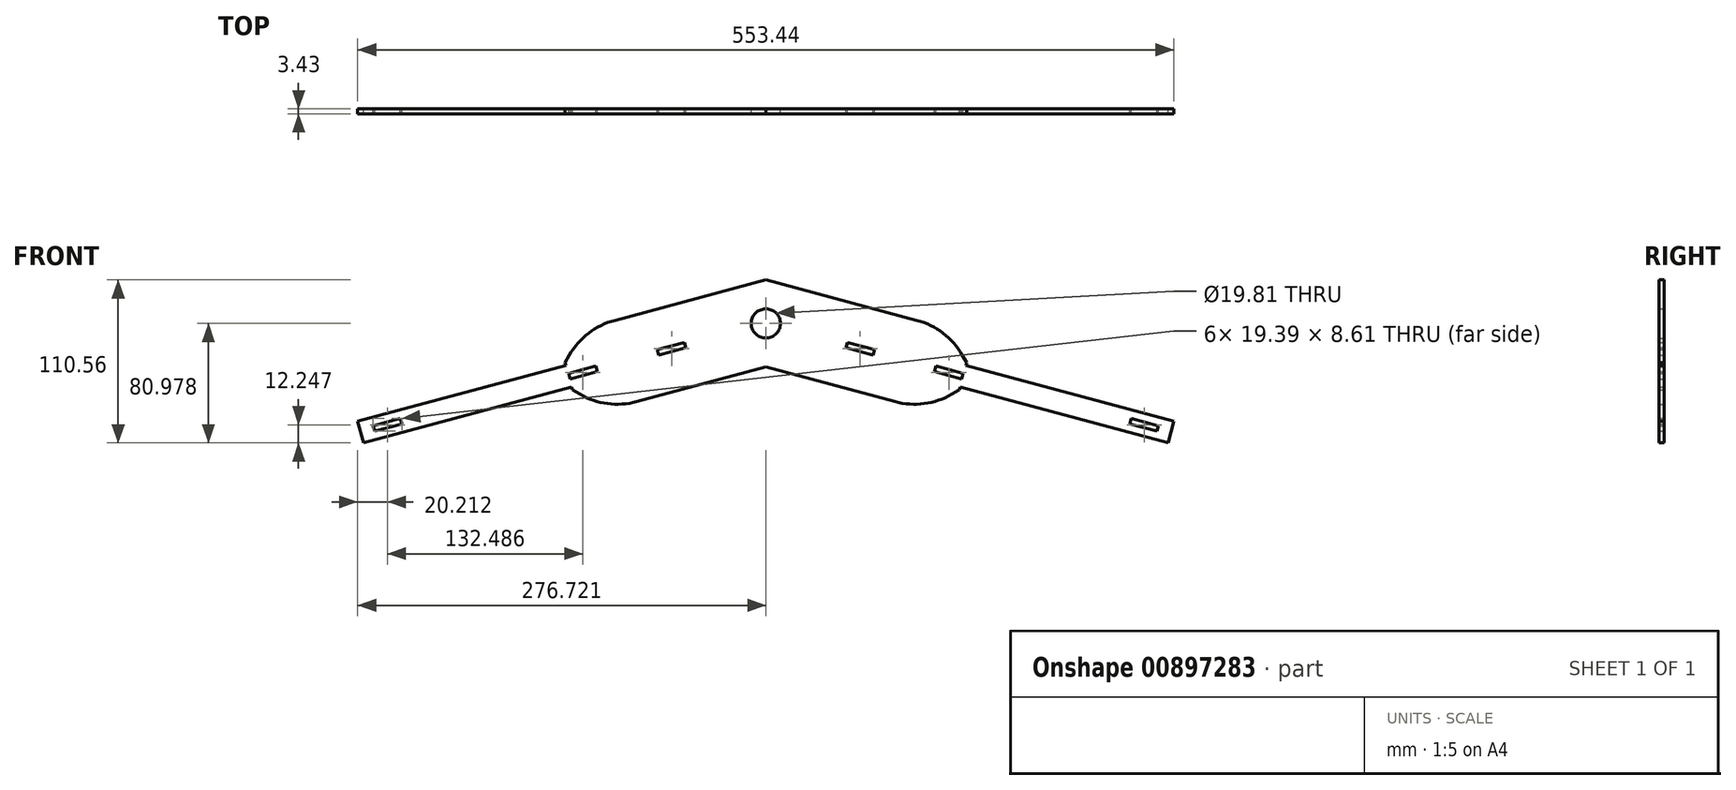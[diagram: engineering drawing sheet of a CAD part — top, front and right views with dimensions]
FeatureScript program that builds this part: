
annotation { "Feature Type Name" : "Feature", "Feature Type Description" : "" }
export const myFeature = defineFeature(function(context is Context, id is Id, definition is map)
    precondition{}
    {
        {
            var Q0;
            Q0=qCreatedBy(makeId("Front.planeOp"),FACE);
            var sketch = newSketch(context, id + "F0", { "sketchPlane" : qUnion([Q0])});
            skLineSegment(sketch, "E0", {"start": v(159.87, 288.6) * mm, "end": v(164.98, 291.55) * mm});
            skArc(sketch, "E1", {"start": v(121.33, 283.52) * mm, "mid": v(141.1, 282.23) * mm, "end": v(159.87, 288.6) * mm});
            skArc(sketch, "E2", {"start": v(-92.33, 288.6) * mm, "mid": v(-73.56, 282.23) * mm, "end": v(-53.79, 283.52) * mm});
            skLineSegment(sketch, "E3", {"start": v(-97.44, 291.55) * mm, "end": v(-92.33, 288.6) * mm});
            skLineSegment(sketch, "E4", {"start": v(-99.42, 315.06) * mm, "end": v(-102.37, 309.95) * mm});
            skArc(sketch, "E5", {"start": v(-68.58, 338.73) * mm, "mid": v(-86.35, 329.96) * mm, "end": v(-99.42, 315.06) * mm});
            skArc(sketch, "E6", {"start": v(166.96, 315.06) * mm, "mid": v(153.9, 329.96) * mm, "end": v(136.12, 338.73) * mm});
            skLineSegment(sketch, "E7", {"start": v(169.91, 309.95) * mm, "end": v(166.96, 315.06) * mm});
            skCircle(sketch, "E8", {"center": v(33.77, 336.57) * mm, "radius": 9.9 * mm});
            skLineSegment(sketch, "E9", {"start": v(-81.54, 307.64) * mm, "end": v(-99.94, 302.71) * mm});
            skLineSegment(sketch, "E10", {"start": v(-99.94, 302.71) * mm, "end": v(-98.96, 299.03) * mm});
            skLineSegment(sketch, "E11", {"start": v(-98.96, 299.03) * mm, "end": v(-80.56, 303.96) * mm});
            skLineSegment(sketch, "E12", {"start": v(-80.56, 303.96) * mm, "end": v(-81.54, 307.64) * mm});
            skLineSegment(sketch, "E13", {"start": v(88.98, 323.75) * mm, "end": v(87.99, 320.07) * mm});
            skLineSegment(sketch, "E14", {"start": v(87.99, 320.07) * mm, "end": v(106.4, 315.14) * mm});
            skLineSegment(sketch, "E15", {"start": v(106.4, 315.14) * mm, "end": v(107.38, 318.82) * mm});
            skLineSegment(sketch, "E16", {"start": v(107.38, 318.82) * mm, "end": v(88.98, 323.75) * mm});
            skLineSegment(sketch, "E17", {"start": v(-21.43, 323.75) * mm, "end": v(-39.84, 318.82) * mm});
            skLineSegment(sketch, "E18", {"start": v(-39.84, 318.82) * mm, "end": v(-38.85, 315.14) * mm});
            skLineSegment(sketch, "E19", {"start": v(-38.85, 315.14) * mm, "end": v(-20.45, 320.07) * mm});
            skLineSegment(sketch, "E20", {"start": v(-20.45, 320.07) * mm, "end": v(-21.43, 323.75) * mm});
            skLineSegment(sketch, "E21", {"start": v(-214.03, 272.14) * mm, "end": v(-232.43, 267.21) * mm});
            skLineSegment(sketch, "E22", {"start": v(-232.43, 267.21) * mm, "end": v(-231.45, 263.53) * mm});
            skLineSegment(sketch, "E23", {"start": v(-231.45, 263.53) * mm, "end": v(-213.04, 268.46) * mm});
            skLineSegment(sketch, "E24", {"start": v(-213.04, 268.46) * mm, "end": v(-214.03, 272.14) * mm});
            skLineSegment(sketch, "E25", {"start": v(166.5, 299.03) * mm, "end": v(167.49, 302.71) * mm});
            skLineSegment(sketch, "E26", {"start": v(167.49, 302.71) * mm, "end": v(149.09, 307.64) * mm});
            skLineSegment(sketch, "E27", {"start": v(149.09, 307.64) * mm, "end": v(148.1, 303.96) * mm});
            skLineSegment(sketch, "E28", {"start": v(148.1, 303.96) * mm, "end": v(166.5, 299.03) * mm});
            skLineSegment(sketch, "E29", {"start": v(281.57, 272.14) * mm, "end": v(280.59, 268.46) * mm});
            skLineSegment(sketch, "E30", {"start": v(280.59, 268.46) * mm, "end": v(298.99, 263.53) * mm});
            skLineSegment(sketch, "E31", {"start": v(298.99, 263.53) * mm, "end": v(299.97, 267.21) * mm});
            skLineSegment(sketch, "E32", {"start": v(299.97, 267.21) * mm, "end": v(281.57, 272.14) * mm});
            skLineSegment(sketch, "E33", {"start": v(136.12, 338.73) * mm, "end": v(33.77, 366.15) * mm});
            skLineSegment(sketch, "E34", {"start": v(169.42, 308.1) * mm, "end": v(169.91, 309.95) * mm});
            skLineSegment(sketch, "E35", {"start": v(310.5, 270.3) * mm, "end": v(169.42, 308.1) * mm});
            skLineSegment(sketch, "E36", {"start": v(306.55, 255.59) * mm, "end": v(310.5, 270.3) * mm});
            skLineSegment(sketch, "E37", {"start": v(165.48, 293.39) * mm, "end": v(306.55, 255.59) * mm});
            skLineSegment(sketch, "E38", {"start": v(164.98, 291.55) * mm, "end": v(165.48, 293.39) * mm});
            skLineSegment(sketch, "E39", {"start": v(33.77, 306.98) * mm, "end": v(121.33, 283.52) * mm});
            skLineSegment(sketch, "E40", {"start": v(-53.79, 283.52) * mm, "end": v(33.77, 306.98) * mm});
            skLineSegment(sketch, "E41", {"start": v(-97.93, 293.39) * mm, "end": v(-97.44, 291.55) * mm});
            skLineSegment(sketch, "E42", {"start": v(-239, 255.59) * mm, "end": v(-97.93, 293.39) * mm});
            skLineSegment(sketch, "E43", {"start": v(-242.95, 270.3) * mm, "end": v(-239, 255.59) * mm});
            skLineSegment(sketch, "E44", {"start": v(-101.88, 308.1) * mm, "end": v(-242.95, 270.3) * mm});
            skLineSegment(sketch, "E45", {"start": v(-102.37, 309.95) * mm, "end": v(-101.88, 308.1) * mm});
            skLineSegment(sketch, "E46", {"start": v(33.77, 366.15) * mm, "end": v(-68.58, 338.73) * mm});
            skSolve(sketch);
        }
        {
            var Q0;
            Q0 = qSketchRegion(id + "F0", true);
            extrude(context, id + "F1", {"entities" : qUnion([Q0]), "depth" : 3.43 * mm, "offsetDistance" : 25.4 * mm});
        }
    });
